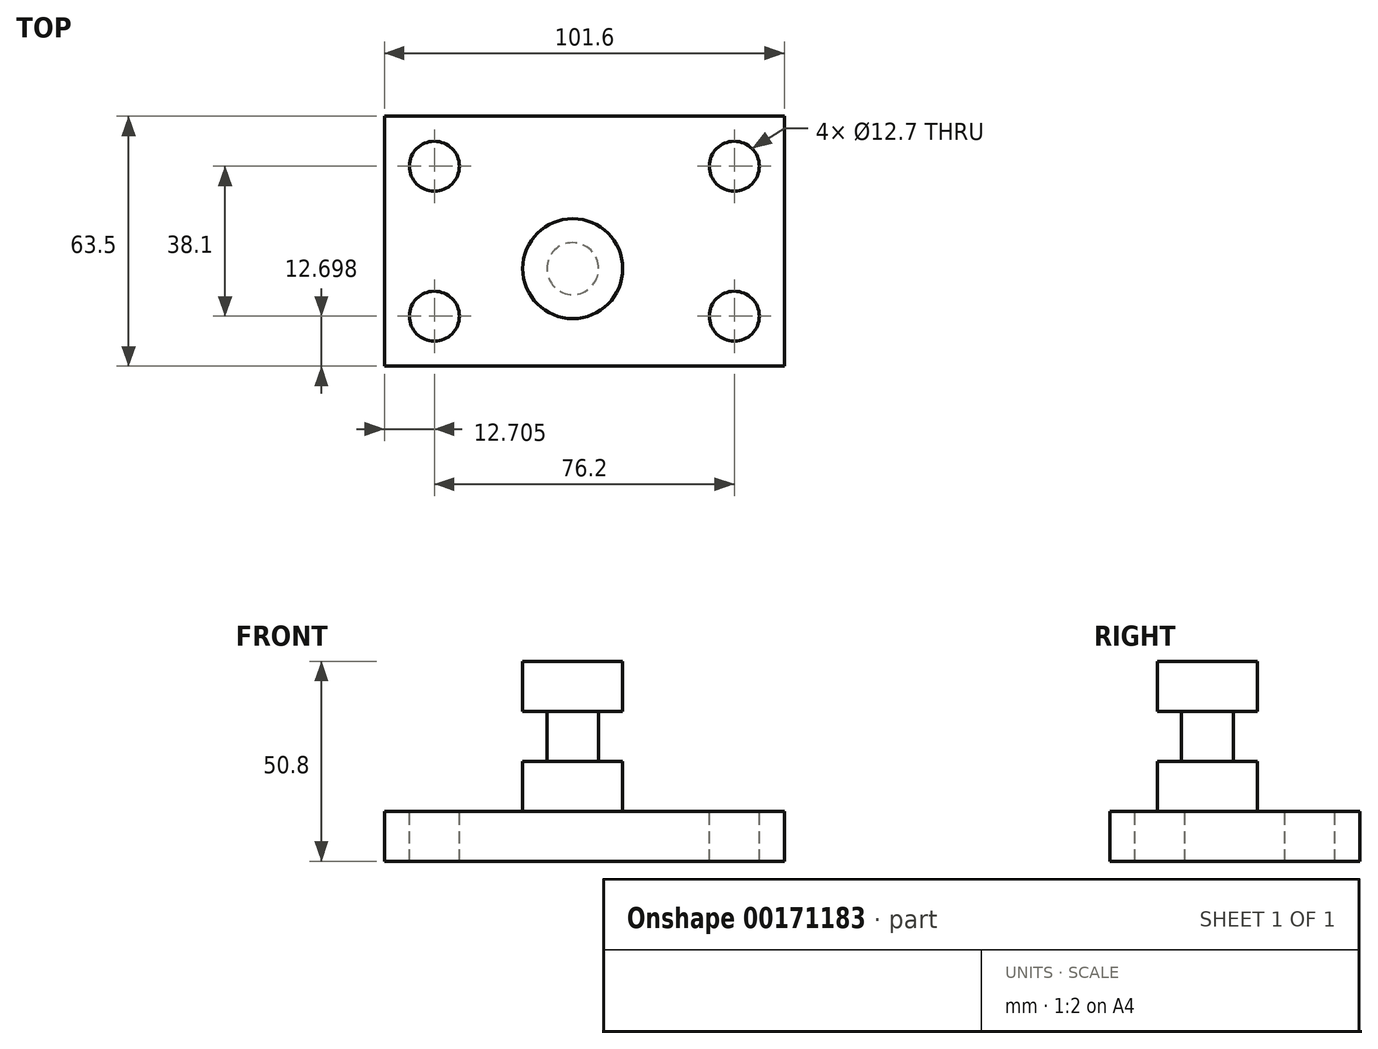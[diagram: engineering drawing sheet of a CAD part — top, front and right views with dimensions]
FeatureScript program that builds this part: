
annotation { "Feature Type Name" : "Feature", "Feature Type Description" : "" }
export const myFeature = defineFeature(function(context is Context, id is Id, definition is map)
    precondition{}
    {
        {
            var Q0;
            Q0=qCreatedBy(makeId("Top.planeOp"),FACE);
            var sketch = newSketch(context, id + "F0", { "sketchPlane" : qUnion([Q0])});
            skLineSegment(sketch, "E0.bottom", {"start": v(-47.87, 38.72) * mm, "end": v(53.73, 38.72) * mm});
            skLineSegment(sketch, "E0.top", {"start": v(-47.87, -24.78) * mm, "end": v(53.73, -24.78) * mm});
            skLineSegment(sketch, "E0.left", {"start": v(-47.87, 38.72) * mm, "end": v(-47.87, -24.78) * mm});
            skLineSegment(sketch, "E0.right", {"start": v(53.73, 38.72) * mm, "end": v(53.73, -24.78) * mm});
            skSolve(sketch);
        }
        {
            var Q0;
            Q0=makeQuery(id+"F0.imprint","IMPRINT",FACE,{"disambiguationData":[TD([[makeQuery(id+"F0.imprint","IMPRINT",EDGE,{"derivedFrom":sQuery(id+"F0.wireOp",EDGE,"E0.bottom")}),-1.0]])]});
            extrude(context, id + "F1", {"entities" : qUnion([Q0]), "depth" : 12.7 * mm});
        }
        {
            var Q0;
            Q0=makeQuery(id+"F1.opExtrude","CAP_FACE",FACE,{"disambiguationData":[OSD([sQuery(id+"F0.wireOp",EDGE,"E0.bottom"),sQuery(id+"F0.wireOp",EDGE,"E0.top"),sQuery(id+"F0.wireOp",EDGE,"E0.left"),sQuery(id+"F0.wireOp",EDGE,"E0.right")])],"isStart":false});
            var sketch = newSketch(context, id + "F2", { "sketchPlane" : qUnion([Q0])});
            skCircle(sketch, "E1", {"center": v(-35.17, 26.02) * mm, "radius": 6.35 * mm});
            skCircle(sketch, "E2", {"center": v(41.03, 26.02) * mm, "radius": 6.35 * mm});
            skCircle(sketch, "E3", {"center": v(-35.17, -12.08) * mm, "radius": 6.35 * mm});
            skCircle(sketch, "E4", {"center": v(41.03, -12.08) * mm, "radius": 6.35 * mm});
            skSolve(sketch);
        }
        {
            var Q0;
            Q0=makeQuery(id+"F2.imprint","IMPRINT",FACE,{"disambiguationData":[TD([[makeQuery(id+"F2.imprint","IMPRINT",EDGE,{"derivedFrom":sQuery(id+"F2.wireOp",EDGE,"E1")}),1.0]])]});
            var Q1;
            Q1=makeQuery(id+"F2.imprint","IMPRINT",FACE,{"disambiguationData":[TD([[makeQuery(id+"F2.imprint","IMPRINT",EDGE,{"derivedFrom":sQuery(id+"F2.wireOp",EDGE,"E3")}),1.0]])]});
            var Q2;
            Q2=makeQuery(id+"F2.imprint","IMPRINT",FACE,{"disambiguationData":[TD([[makeQuery(id+"F2.imprint","IMPRINT",EDGE,{"derivedFrom":sQuery(id+"F2.wireOp",EDGE,"E4")}),1.0]])]});
            var Q3;
            Q3=makeQuery(id+"F2.imprint","IMPRINT",FACE,{"disambiguationData":[TD([[makeQuery(id+"F2.imprint","IMPRINT",EDGE,{"derivedFrom":sQuery(id+"F2.wireOp",EDGE,"E2")}),1.0]])]});
            extrude(context, id + "F3", {"entities" : qUnion([Q0, Q1, Q2, Q3]), "operationType" : NewBodyOperationType.REMOVE, "endBound" : BoundingType.THROUGH_ALL, "oppositeDirection" : true, "depth" : 25.4 * mm});
        }
        {
            var Q0;
            Q0=qCreatedBy(makeId("Front.planeOp"),FACE);
            var sketch = newSketch(context, id + "F4", { "sketchPlane" : qUnion([Q0])});
            skLineSegment(sketch, "E5.bottom", {"start": v(0, 50.8) * mm, "end": v(-12.7, 50.8) * mm});
            skLineSegment(sketch, "E5.top", {"start": v(0, 12.7) * mm, "end": v(-12.7, 12.7) * mm});
            skLineSegment(sketch, "E5.left", {"start": v(0, 50.8) * mm, "end": v(0, 12.7) * mm});
            skLineSegment(sketch, "E5.right", {"start": v(-12.7, 50.8) * mm, "end": v(-12.7, 12.7) * mm});
            skSolve(sketch);
        }
        {
            var Q0;
            Q0=makeQuery(id+"F4.imprint","IMPRINT",FACE,{"disambiguationData":[TD([[makeQuery(id+"F4.imprint","IMPRINT",EDGE,{"derivedFrom":sQuery(id+"F4.wireOp",EDGE,"E5.bottom")}),1.0]])]});
            var Q1;
            Q1=sQuery(id+"F4.wireOp",EDGE,"E5.left");
            revolve(context, id + "F5", {"operationType" : NewBodyOperationType.ADD, "entities" : qUnion([Q0]), "axis" : qUnion([Q1]), "revolveType" : RevolveType.FULL});
        }
        {
            var Q0;
            Q0=qCreatedBy(makeId("Front.planeOp"),FACE);
            var sketch = newSketch(context, id + "F6", { "sketchPlane" : qUnion([Q0])});
            skLineSegment(sketch, "E6.bottom", {"start": v(-31.95, 38.1) * mm, "end": v(-6.58, 38.1) * mm});
            skLineSegment(sketch, "E6.top", {"start": v(-31.95, 25.4) * mm, "end": v(-6.58, 25.4) * mm});
            skLineSegment(sketch, "E6.left", {"start": v(-31.95, 38.1) * mm, "end": v(-31.95, 25.4) * mm});
            skLineSegment(sketch, "E6.right", {"start": v(-6.58, 38.1) * mm, "end": v(-6.58, 25.4) * mm});
            skLineSegment(sketch, "E7", {"start": v(0, 0) * mm, "end": v(0, 52.9) * mm});
            skSolve(sketch);
        }
        {
            var Q0;
            Q0=makeQuery(id+"F6.imprint","IMPRINT",FACE,{"disambiguationData":[TD([[makeQuery(id+"F6.imprint","IMPRINT",EDGE,{"derivedFrom":sQuery(id+"F6.wireOp",EDGE,"E6.bottom")}),-1.0]])]});
            var Q1;
            Q1=sQuery(id+"F6.wireOp",EDGE,"E7");
            revolve(context, id + "F7", {"operationType" : NewBodyOperationType.REMOVE, "entities" : qUnion([Q0]), "axis" : qUnion([Q1]), "revolveType" : RevolveType.FULL, "oppositeDirection" : true});
        }
    });
